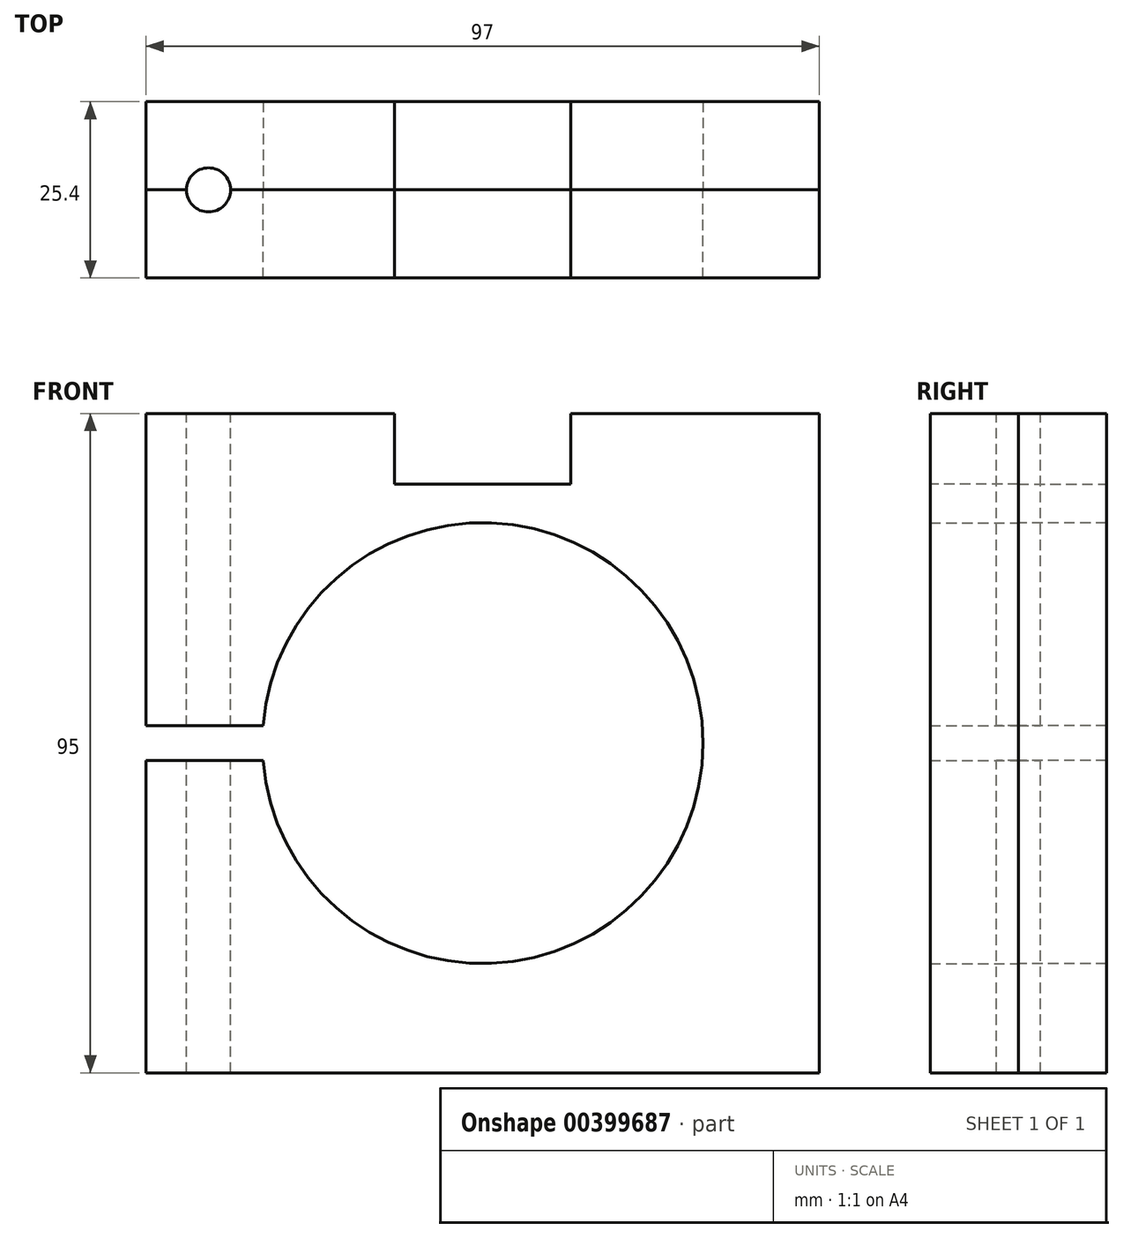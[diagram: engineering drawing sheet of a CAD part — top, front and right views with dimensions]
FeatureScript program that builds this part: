
annotation { "Feature Type Name" : "Feature", "Feature Type Description" : "" }
export const myFeature = defineFeature(function(context is Context, id is Id, definition is map)
    precondition{}
    {
        {
            var Q0;
            Q0=qCreatedBy(makeId("Front.planeOp"),FACE);
            var sketch = newSketch(context, id + "F0", { "sketchPlane" : qUnion([Q0])});
            skArc(sketch, "E0", {"start": v(-9.72, 30.23) * mm, "mid": v(-31.75, 0) * mm, "end": v(-9.72, -30.23) * mm});
            skLineSegment(sketch, "E1.bottom", {"start": v(-48.5, 47.5) * mm, "end": v(48.5, 47.5) * mm});
            skLineSegment(sketch, "E1.top", {"start": v(-48.5, -47.5) * mm, "end": v(48.5, -47.5) * mm});
            skLineSegment(sketch, "E1.left", {"start": v(-48.5, 47.5) * mm, "end": v(-48.5, -47.5) * mm});
            skLineSegment(sketch, "E1.right", {"start": v(48.5, 47.5) * mm, "end": v(48.5, -47.5) * mm});
            skLineSegment(sketch, "E2", {"start": v(0, 0) * mm, "end": v(-48.5, 0) * mm, "construction": true});
            skLineSegment(sketch, "E3", {"start": v(-48.5, 2.5) * mm, "end": v(-31.65, 2.5) * mm});
            skLineSegment(sketch, "E4.MirrorCS", {"start": v(-48.5, -2.5) * mm, "end": v(-31.65, -2.5) * mm});
            skPoint(sketch, "E5.orphan", {"position": v(-26.24, 2.5) * mm});
            skPoint(sketch, "E6.orphan", {"position": v(-26.24, -2.5) * mm});
            skLineSegment(sketch, "E7", {"start": v(-9.72, 30.23) * mm, "end": v(9.72, 30.23) * mm});
            skLineSegment(sketch, "E8.MirrorCS", {"start": v(-9.72, -30.23) * mm, "end": v(9.72, -30.23) * mm});
            skArc(sketch, "E9.trimOffspring", {"start": v(9.72, -30.23) * mm, "mid": v(31.75, 0) * mm, "end": v(9.72, 30.23) * mm});
            skCircle(sketch, "E10", {"center": v(0, 0) * mm, "radius": 31.75 * mm});
            skSolve(sketch);
        }
        {
            var Q0;
            {var subQ1=sQuery(id+"F0.wireOp",EDGE,"E1.bottom");Q0=makeQuery(id+"F0.imprint","IMPRINT",FACE,{"disambiguationData":[TD([[makeQuery(id+"F0.imprint","IMPRINT",EDGE,{"derivedFrom":subQ1}),-1.0]])]});}
            extrude(context, id + "F1", {"entities" : qUnion([Q0]), "depth" : 12.7 * mm});
        }
        {
            var Q0;
            Q0=makeQuery(id+"F1.opExtrude","SWEPT_FACE",FACE,{"disambiguationData":[OSD([sQuery(id+"F0.wireOp",EDGE,"E1.bottom")])]});
            var sketch = newSketch(context, id + "F2", { "sketchPlane" : qUnion([Q0])});
            skLineSegment(sketch, "E11", {"start": v(-12.7, 0) * mm, "end": v(-12.7, -12.7) * mm});
            skLineSegment(sketch, "E12", {"start": v(0, 0) * mm, "end": v(0, -12.7) * mm, "construction": true});
            skLineSegment(sketch, "E13.MirrorCS", {"start": v(12.7, 0) * mm, "end": v(12.7, -12.7) * mm});
            skSolve(sketch);
        }
        {
            var Q0;
            {var subQ0=sQuery(id+"F2.wireOp",EDGE,"E11");Q0=makeQuery(id+"F2.imprint","IMPRINT",FACE,{"disambiguationData":[TD([[makeQuery(id+"F2.imprint","IMPRINT",EDGE,{"derivedFrom":subQ0}),1.0]])]});}
            extrude(context, id + "F3", {"entities" : qUnion([Q0]), "operationType" : NewBodyOperationType.REMOVE, "oppositeDirection" : true, "depth" : 10.16 * mm});
        }
        {
            var Q0;
            Q0=makeQuery(id+"F1.opExtrude","SWEPT_BODY",BODY,{"disambiguationData":[OSD([sQuery(id+"F0.wireOp",EDGE,"E1.bottom"),sQuery(id+"F0.wireOp",EDGE,"E1.top"),sQuery(id+"F0.wireOp",EDGE,"E1.left"),sQuery(id+"F0.wireOp",EDGE,"E1.right"),sQuery(id+"F0.wireOp",EDGE,"E3"),sQuery(id+"F0.wireOp",EDGE,"E4.MirrorCS"),sQuery(id+"F0.wireOp",EDGE,"E10")])]});
            var Q1;
            Q1=qCreatedBy(makeId("Front.planeOp"),FACE);
            mirror(context, id + "F4", {"entities" : qUnion([Q0]), "mirrorPlane" : qUnion([Q1])});
        }
        {
            var Q0;
            {var subQ6=sQuery(id+"F0.wireOp",EDGE,"E1.bottom");Q0=makeQuery(id+"F4.opPattern","COPY",FACE,{"derivedFrom":makeQuery(id+"F3.boolean.opBoolean","SPLIT",FACE,{"disambiguationData":[TD([makeQuery(id+"F3.opExtrude","SWEPT_FACE",FACE,{"disambiguationData":[OSD([sQuery(id+"F2.wireOp",EDGE,"E11")])]})])],"derivedFrom":makeQuery(id+"F1.opExtrude","SWEPT_FACE",FACE,{"disambiguationData":[OSD([subQ6])]})}),"instanceName":"1"});}
            var sketch = newSketch(context, id + "F5", { "sketchPlane" : qUnion([Q0])});
            skPoint(sketch, "E14", {"position": v(-39.5, 0) * mm});
            skSolve(sketch);
        }
        {
            var Q0;
            Q0=sQuery(id+"F5.wireOp",VERTEX,"E14");
            var Q1;
            Q1=makeQuery(id+"F1.opExtrude","SWEPT_BODY",BODY,{"disambiguationData":[OSD([sQuery(id+"F0.wireOp",EDGE,"E1.bottom"),sQuery(id+"F0.wireOp",EDGE,"E1.top"),sQuery(id+"F0.wireOp",EDGE,"E1.left"),sQuery(id+"F0.wireOp",EDGE,"E1.right"),sQuery(id+"F0.wireOp",EDGE,"E3"),sQuery(id+"F0.wireOp",EDGE,"E4.MirrorCS"),sQuery(id+"F0.wireOp",EDGE,"E10")])]});
            var Q2;
            Q2=makeQuery(id+"F4.opPattern","COPY",BODY,{"derivedFrom":makeQuery(id+"F1.opExtrude","SWEPT_BODY",BODY,{"disambiguationData":[OSD([sQuery(id+"F0.wireOp",EDGE,"E1.bottom"),sQuery(id+"F0.wireOp",EDGE,"E1.top"),sQuery(id+"F0.wireOp",EDGE,"E1.left"),sQuery(id+"F0.wireOp",EDGE,"E1.right"),sQuery(id+"F0.wireOp",EDGE,"E3"),sQuery(id+"F0.wireOp",EDGE,"E4.MirrorCS"),sQuery(id+"F0.wireOp",EDGE,"E10")])]}),"instanceName":"1"});
            hole(context, id + "F6", {"style" : HoleStyle.SIMPLE, "endStyle" : HoleEndStyle.THROUGH, "holeDiameter" : 6.35 * mm, "isTappedThrough" : true, "tappedDepth" : 12.7 * mm, "tapClearance" : 3, "locations" : qUnion([Q0]), "scope" : qUnion([Q1, Q2])});
        }
    });
